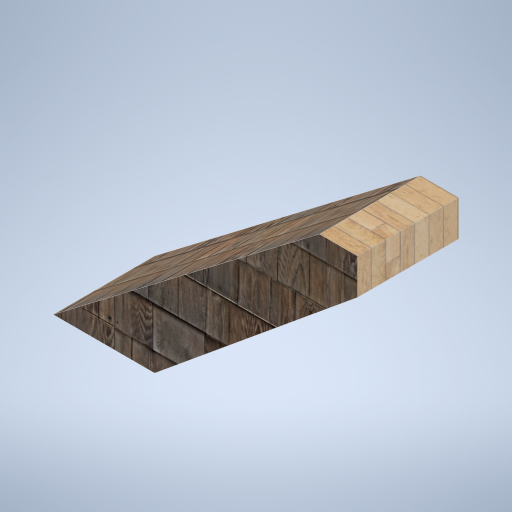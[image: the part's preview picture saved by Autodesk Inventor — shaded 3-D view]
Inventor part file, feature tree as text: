
AUTODESK INVENTOR PART (.ipt)
format: ipt  version: 2024.2 (Build 282272000, 272)  size: 328,192 bytes
history: native  units: in
note: dims shown in document units (in); Inventor stores cm internally (conversion verified against a paired STEP export)
features: other x3, sketch x1
ambient origin geometry x8: Origin, YZ Plane, XZ Plane, XY Plane, X Axis, Y Axis, Z Axis, Center Point
bodies: Body1 (feature_tree)
feature tree (4):
  other  "frame_rib_02.ipt"
  other  "Solid3::frame_rib_02.ipt"
  other  "TaggingFeature1"
  sketch  "Sketch1"  dims[d0=0.3937in]
